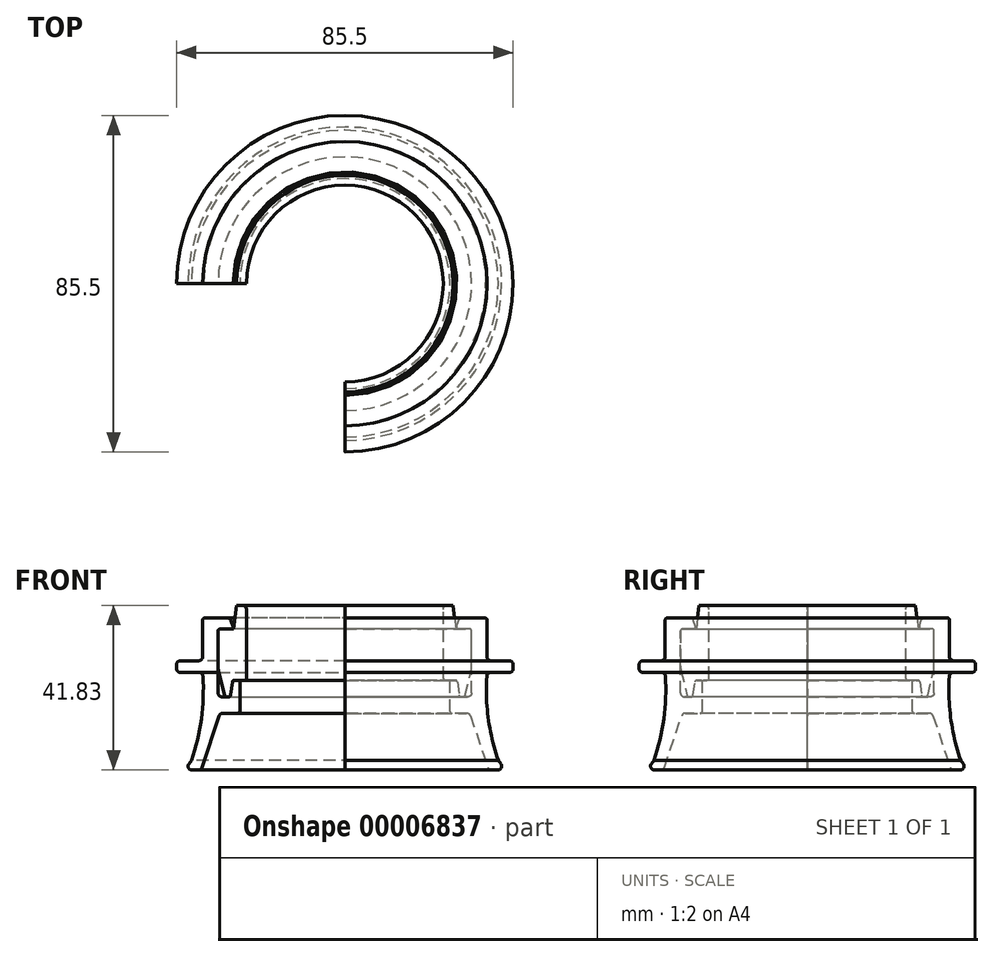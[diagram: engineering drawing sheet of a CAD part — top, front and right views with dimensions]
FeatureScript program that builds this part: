
annotation { "Feature Type Name" : "Feature", "Feature Type Description" : "" }
export const myFeature = defineFeature(function(context is Context, id is Id, definition is map)
    precondition{}
    {
        {
            var Q0;
            Q0=qCreatedBy(makeId("Front.planeOp"),FACE);
            var sketch = newSketch(context, id + "F0", { "sketchPlane" : qUnion([Q0])});
            skLineSegment(sketch, "E0", {"start": v(0, 0) * mm, "end": v(-25, 0) * mm});
            skLineSegment(sketch, "E1", {"start": v(-25, 0) * mm, "end": v(-25, 6) * mm});
            skLineSegment(sketch, "E2", {"start": v(-25, 6) * mm, "end": v(-27.5, 6) * mm});
            skLineSegment(sketch, "E3", {"start": v(-28.22, 0) * mm, "end": v(-32.22, 0) * mm});
            skLineSegment(sketch, "E4", {"start": v(-32.22, 0) * mm, "end": v(-32.22, -10) * mm});
            skLineSegment(sketch, "E5", {"start": v(0, 0) * mm, "end": v(0, -8.07) * mm});
            skLineSegment(sketch, "E6", {"start": v(-27.5, 6) * mm, "end": v(-28.22, 0) * mm});
            skLineSegment(sketch, "E7", {"start": v(-32.22, -10) * mm, "end": v(-30.48, -17.21) * mm});
            skLineSegment(sketch, "E8", {"start": v(-30.48, -17.21) * mm, "end": v(-29.06, -17.21) * mm});
            skLineSegment(sketch, "E9", {"start": v(-29.06, -17.21) * mm, "end": v(-28.5, -13) * mm});
            skLineSegment(sketch, "E10", {"start": v(-28.5, -13) * mm, "end": v(-25, -13) * mm});
            skLineSegment(sketch, "E11", {"start": v(-25, -13) * mm, "end": v(-25, 0) * mm});
            skLineSegment(sketch, "E12", {"start": v(-28.22, 0) * mm, "end": v(-29.12, 2.8) * mm});
            skLineSegment(sketch, "E13", {"start": v(-29.12, 2.8) * mm, "end": v(-36.12, 2.8) * mm});
            skLineSegment(sketch, "E14", {"start": v(-36.12, 2.8) * mm, "end": v(-36.12, -8.04) * mm});
            skLineSegment(sketch, "E15", {"start": v(-36.12, -8.04) * mm, "end": v(-42.75, -8.04) * mm});
            skLineSegment(sketch, "E16", {"start": v(-42.75, -8.04) * mm, "end": v(-42.75, -11.04) * mm});
            skLineSegment(sketch, "E17", {"start": v(-42.75, -11.04) * mm, "end": v(-36.12, -11.04) * mm});
            skLineSegment(sketch, "E18", {"start": v(-38.98, -33.4) * mm, "end": v(-39.83, -34.48) * mm});
            skLineSegment(sketch, "E19", {"start": v(-39.83, -34.48) * mm, "end": v(-39.83, -35.83) * mm});
            skLineSegment(sketch, "E20", {"start": v(-39.83, -35.83) * mm, "end": v(-36.55, -35.83) * mm});
            skLineSegment(sketch, "E21", {"start": v(-36.55, -35.83) * mm, "end": v(-31.68, -21.38) * mm});
            skLineSegment(sketch, "E22", {"start": v(-31.68, -21.38) * mm, "end": v(-26.68, -21.38) * mm});
            skLineSegment(sketch, "E23", {"start": v(-26.68, -21.38) * mm, "end": v(-26.68, -13) * mm});
            skLineSegment(sketch, "E24", {"start": v(-26.68, -13) * mm, "end": v(-28.5, -13) * mm});
            skLineSegment(sketch, "E25", {"start": v(-29.06, -17.21) * mm, "end": v(-32.22, -17.21) * mm});
            skLineSegment(sketch, "E26", {"start": v(-32.22, -17.21) * mm, "end": v(-32.22, -10) * mm});
            skLineSegment(sketch, "E27", {"start": v(-32.22, 0) * mm, "end": v(-28.22, 0) * mm});
            skArc(sketch, "E28", {"start": v(-38.98, -33.4) * mm, "mid": v(-36.4, -22.37) * mm, "end": v(-36.12, -11.04) * mm});
            skSolve(sketch);
        }
        {
            var Q0;
            Q0=makeQuery(id+"F0.imprint","IMPRINT",FACE,{"disambiguationData":[TD([[makeQuery(id+"F0.imprint","IMPRINT",EDGE,{"derivedFrom":sQuery(id+"F0.wireOp",EDGE,"E1")}),1.0]])]});
            var Q1;
            Q1=sQuery(id+"F0.wireOp",EDGE,"E5");
            revolve(context, id + "F1", {"entities" : qUnion([Q0]), "axis" : qUnion([Q1]), "revolveType" : RevolveType.ONE_DIRECTION, "angle" : 270 * degree});
        }
        {
            var Q0;
            Q0=makeQuery(id+"F0.imprint","IMPRINT",FACE,{"disambiguationData":[TD([[makeQuery(id+"F0.imprint","IMPRINT",EDGE,{"derivedFrom":sQuery(id+"F0.wireOp",EDGE,"E4")}),-1.0]])]});
            var Q1;
            Q1=sQuery(id+"F0.wireOp",EDGE,"E5");
            revolve(context, id + "F2", {"entities" : qUnion([Q0]), "axis" : qUnion([Q1]), "revolveType" : RevolveType.ONE_DIRECTION, "angle" : 270 * degree});
        }
        {
            var Q0;
            Q0=makeQuery(id+"F1.opRevolve","SWEPT_EDGE",EDGE,{"disambiguationData":[OSD([sQuery(id+"F0.wireOp",EDGE,"E1"),sQuery(id+"F0.wireOp",EDGE,"E2")])]});
            fillet(context, id + "F3", {"entities" : qUnion([Q0]), "radius" : 1 * mm, "tangentPropagation" : true, "allowEdgeOverflow" : false});
        }
        {
            var Q0;
            Q0=makeQuery(id+"F2.opRevolve","SWEPT_EDGE",EDGE,{"disambiguationData":[OSD([sQuery(id+"F0.wireOp",EDGE,"E12"),sQuery(id+"F0.wireOp",EDGE,"E13")])]});
            fillet(context, id + "F4", {"entities" : qUnion([Q0]), "radius" : 1 * mm, "tangentPropagation" : true, "allowEdgeOverflow" : false});
        }
        {
            var Q0;
            Q0=makeQuery(id+"F2.opRevolve","SWEPT_EDGE",EDGE,{"disambiguationData":[OSD([sQuery(id+"F0.wireOp",EDGE,"E13"),sQuery(id+"F0.wireOp",EDGE,"E14")])]});
            fillet(context, id + "F5", {"entities" : qUnion([Q0]), "radius" : 0.5 * mm, "tangentPropagation" : true, "allowEdgeOverflow" : false});
        }
        {
            var Q0;
            Q0=makeQuery(id+"F2.opRevolve","SWEPT_EDGE",EDGE,{"disambiguationData":[OSD([sQuery(id+"F0.wireOp",EDGE,"E14"),sQuery(id+"F0.wireOp",EDGE,"E15")])]});
            var Q1;
            Q1=makeQuery(id+"F2.opRevolve","SWEPT_EDGE",EDGE,{"disambiguationData":[OSD([sQuery(id+"F0.wireOp",EDGE,"E17"),sQuery(id+"F0.wireOp",EDGE,"37022625-18a0-4200-be37-71287813a7e6")])]});
            var Q2;
            Q2=makeQuery(id+"F2.opRevolve","SWEPT_EDGE",EDGE,{"disambiguationData":[OSD([sQuery(id+"F0.wireOp",EDGE,"E21"),sQuery(id+"F0.wireOp",EDGE,"E22")])]});
            var Q3;
            Q3=makeQuery(id+"F2.opRevolve","SWEPT_EDGE",EDGE,{"disambiguationData":[OSD([sQuery(id+"F0.wireOp",EDGE,"E25"),sQuery(id+"F0.wireOp",EDGE,"E26")])]});
            fillet(context, id + "F6", {"entities" : qUnion([Q0, Q1, Q2, Q3]), "radius" : 1 * mm, "tangentPropagation" : true, "allowEdgeOverflow" : false});
        }
        {
            var Q0;
            Q0=makeQuery(id+"F2.opRevolve","SWEPT_EDGE",EDGE,{"disambiguationData":[OSD([sQuery(id+"F0.wireOp",EDGE,"E15"),sQuery(id+"F0.wireOp",EDGE,"E16")])]});
            var Q1;
            Q1=makeQuery(id+"F2.opRevolve","SWEPT_EDGE",EDGE,{"disambiguationData":[OSD([sQuery(id+"F0.wireOp",EDGE,"E16"),sQuery(id+"F0.wireOp",EDGE,"E17")])]});
            fillet(context, id + "F7", {"entities" : qUnion([Q0, Q1]), "radius" : 1 * mm, "tangentPropagation" : true, "allowEdgeOverflow" : false});
        }
        {
            var Q0;
            Q0=makeQuery(id+"F2.opRevolve","SWEPT_EDGE",EDGE,{"disambiguationData":[OSD([sQuery(id+"F0.wireOp",EDGE,"E18"),sQuery(id+"F0.wireOp",EDGE,"E19")])]});
            var Q1;
            Q1=makeQuery(id+"F2.opRevolve","SWEPT_EDGE",EDGE,{"disambiguationData":[OSD([sQuery(id+"F0.wireOp",EDGE,"E19"),sQuery(id+"F0.wireOp",EDGE,"E20")])]});
            var Q2;
            Q2=makeQuery(id+"F2.opRevolve","SWEPT_EDGE",EDGE,{"disambiguationData":[OSD([sQuery(id+"F0.wireOp",EDGE,"E20"),sQuery(id+"F0.wireOp",EDGE,"E21")])]});
            fillet(context, id + "F8", {"entities" : qUnion([Q0, Q1, Q2]), "radius" : 1 * mm, "tangentPropagation" : true, "allowEdgeOverflow" : false});
        }
        {
            var Q0;
            Q0=makeQuery(id+"F1.opRevolve","SWEPT_EDGE",EDGE,{"disambiguationData":[OSD([sQuery(id+"F0.wireOp",EDGE,"E4"),sQuery(id+"F0.wireOp",EDGE,"E7"),sQuery(id+"F0.wireOp",EDGE,"E26")])]});
            fillet(context, id + "F9", {"entities" : qUnion([Q0]), "radius" : 5 * mm, "tangentPropagation" : true, "allowEdgeOverflow" : false});
        }
        {
            var Q0;
            Q0=makeQuery(id+"F1.opRevolve","SWEPT_EDGE",EDGE,{"disambiguationData":[OSD([sQuery(id+"F0.wireOp",EDGE,"E9"),sQuery(id+"F0.wireOp",EDGE,"E25")])]});
            var Q1;
            Q1=makeQuery(id+"F1.opRevolve","SWEPT_EDGE",EDGE,{"disambiguationData":[OSD([sQuery(id+"F0.wireOp",EDGE,"E7"),sQuery(id+"F0.wireOp",EDGE,"E25")])]});
            var Q2;
            Q2=makeQuery(id+"F1.opRevolve","SWEPT_EDGE",EDGE,{"disambiguationData":[OSD([sQuery(id+"F0.wireOp",EDGE,"E10"),sQuery(id+"F0.wireOp",EDGE,"E11")])]});
            var Q3;
            Q3=makeQuery(id+"F1.opRevolve","SWEPT_EDGE",EDGE,{"disambiguationData":[OSD([sQuery(id+"F0.wireOp",EDGE,"E9"),sQuery(id+"F0.wireOp",EDGE,"E24")])]});
            fillet(context, id + "F10", {"entities" : qUnion([Q0, Q1, Q2, Q3]), "radius" : 0.5 * mm, "tangentPropagation" : true, "allowEdgeOverflow" : false});
        }
        {
            var Q0;
            Q0=makeQuery(id+"F2.opRevolve","SWEPT_EDGE",EDGE,{"disambiguationData":[OSD([sQuery(id+"F0.wireOp",EDGE,"E22"),sQuery(id+"F0.wireOp",EDGE,"E23")])]});
            var Q1;
            Q1=makeQuery(id+"F2.opRevolve","SWEPT_EDGE",EDGE,{"disambiguationData":[OSD([sQuery(id+"F0.wireOp",EDGE,"E10"),sQuery(id+"F0.wireOp",EDGE,"E23"),sQuery(id+"F0.wireOp",EDGE,"E24")])]});
            var Q2;
            Q2=makeQuery(id+"F2.opRevolve","SWEPT_EDGE",EDGE,{"disambiguationData":[OSD([sQuery(id+"F0.wireOp",EDGE,"E9"),sQuery(id+"F0.wireOp",EDGE,"E24")])]});
            var Q3;
            Q3=makeQuery(id+"F2.opRevolve","SWEPT_EDGE",EDGE,{"disambiguationData":[OSD([sQuery(id+"F0.wireOp",EDGE,"E6"),sQuery(id+"F0.wireOp",EDGE,"E12"),sQuery(id+"F0.wireOp",EDGE,"E27")])]});
            fillet(context, id + "F11", {"entities" : qUnion([Q0, Q1, Q2, Q3]), "radius" : 0.5 * mm, "tangentPropagation" : true, "allowEdgeOverflow" : false});
        }
        {
            var Q0;
            Q0=makeQuery(id+"F2.opRevolve","SWEPT_EDGE",EDGE,{"disambiguationData":[OSD([sQuery(id+"F0.wireOp",EDGE,"E4"),sQuery(id+"F0.wireOp",EDGE,"E27")])]});
            var Q1;
            Q1=makeQuery(id+"F2.opRevolve","SWEPT_EDGE",EDGE,{"disambiguationData":[OSD([sQuery(id+"F0.wireOp",EDGE,"E9"),sQuery(id+"F0.wireOp",EDGE,"E25")])]});
            var Q2;
            Q2=makeQuery(id+"F1.opRevolve","SWEPT_EDGE",EDGE,{"disambiguationData":[OSD([sQuery(id+"F0.wireOp",EDGE,"E4"),sQuery(id+"F0.wireOp",EDGE,"E27")])]});
            fillet(context, id + "F12", {"entities" : qUnion([Q0, Q1, Q2]), "radius" : 0.5 * mm, "tangentPropagation" : true, "allowEdgeOverflow" : false});
        }
    });
